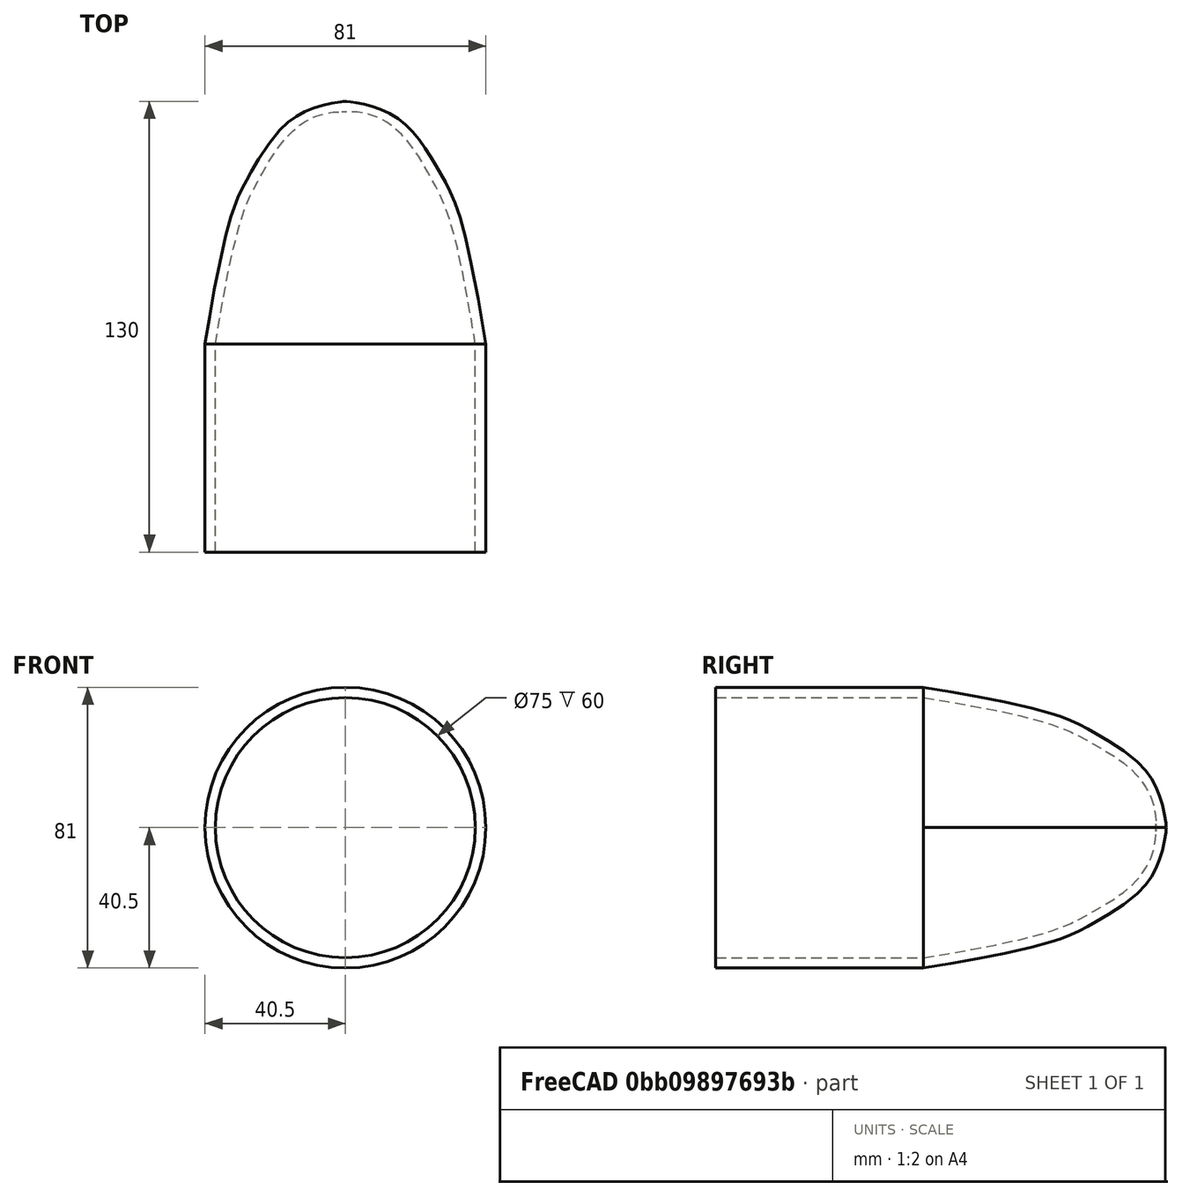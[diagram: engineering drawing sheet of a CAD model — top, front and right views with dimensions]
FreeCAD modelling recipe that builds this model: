
FCSTD DOCUMENT  (FreeCAD 0.18R16131 (Git))
Label: S200_Head
License: All rights reserved
LicenseURL: http://en.wikipedia.org/wiki/All_rights_reserved
objects: Sketcher::SketchObject×1, PartDesign::Revolution×1, PartDesign::Body×1
note: 4 computed .brp shape members not serialized (recipe doc carries the construction recipe); baked Part::Feature solids carry a one-line shape summary decoded from their .brp

FEATURE [Sketcher::SketchObject] Sketch
  MapMode = 5
  Support = -> [XY_Plane]
  sketch-geometry (24):
    g0: LineSegment StartX=37.5 StartY=0 StartZ=0 EndX=40.5 EndY=0 EndZ=0
    g1: LineSegment StartX=37.5 StartY=0 StartZ=0 EndX=37.5 EndY=60 EndZ=0
    g2: LineSegment StartX=40.5 StartY=0 StartZ=0 EndX=40.5 EndY=60 EndZ=0
    g3-g8: Circle [constr] x6 (B-spline internal-alignment scaffolding for g9; pole/knot coordinates omitted)
    g9: BSplineCurve PolesCount=6 KnotsCount=4 Degree=3 IsPeriodic=0
    g10-g13: GeomPoint [constr] x4 (B-spline internal-alignment scaffolding for g9; pole/knot coordinates omitted)
    g14-g18: Circle [constr] x5 (B-spline internal-alignment scaffolding for g19; pole/knot coordinates omitted)
    g19: BSplineCurve PolesCount=5 KnotsCount=3 Degree=3 IsPeriodic=0
    g20: GeomPoint [constr] X=37.5 Y=60 Z=0
    g21: GeomPoint [constr] X=24.3396 Y=108.63 Z=0
    g22: GeomPoint [constr] X=0 Y=127 Z=0
    g23: LineSegment StartX=0 StartY=130 StartZ=0 EndX=0 EndY=127 EndZ=0
  constraints (38):
    c: PointOnObject(g0,g-1)
    c: Horizontal(g0)
    c: Coincident(g1,g0)
    c: Vertical(g1)
    c: Coincident(g2,g0)
    c: Vertical(g2)
    c: DistanceX(g0,g0) = 3
    c: Distance(g-1,g0) = 40.5
    c: DistanceY(g2,g2) = 60
    c: Equal(g2,g1)
    c: Coincident(g9,g2)
    c: Radius(g3) = 3
    c: Equal(g3, g4-g7) x4
    c: PointOnObject(g7,g-2)
    c: Equal(g3,g8)
    c: Coincident(g9,g7)
    c: InternalAlignment(g3-g8 -> g9) x6
    c: InternalAlignment(g10-g13 -> g9) x4
    c: DistanceY(g2,g9) = 70
    c: DistanceY(g2,g4) = 37
    c: DistanceX(g4,g2) = 6
    c: DistanceY(g4,g5) = 10
    c: DistanceX(g5,g4) = 6
    c: DistanceY(g5,g6) = 22
    c: DistanceX(g6,g5) = 12
    c: Coincident(g19,g1)
    c: Radius(g14) = 6
    c: Equal(g14, g15-g18) x4
    c: PointOnObject(g19,g-2)
    c: InternalAlignment(g14-g18 -> g19) x5
    c: InternalAlignment(g20,g19)
    c: InternalAlignment(g21,g19)
    c: Distance(g15,g4) = 3
    c: Distance(g17,g6) = 3
    c: Distance(g19,g9) = 3
    c: Distance(g5,g16) = 3
    c: Coincident(g23,g9)
    c: Coincident(g23,g19)
FEATURE [PartDesign::Revolution] Revolution
  Angle = 360
  Axis = (1e-16,1,-1e-16)
  Base = (0,0,0)
  Profile = -> Sketch
  ReferenceAxis = -> Y_Axis
  Reversed = true
FEATURE [PartDesign::Body] Body
  Group = -> [Sketch,Revolution]
  Origin = -> Origin
  Tip = -> Revolution
